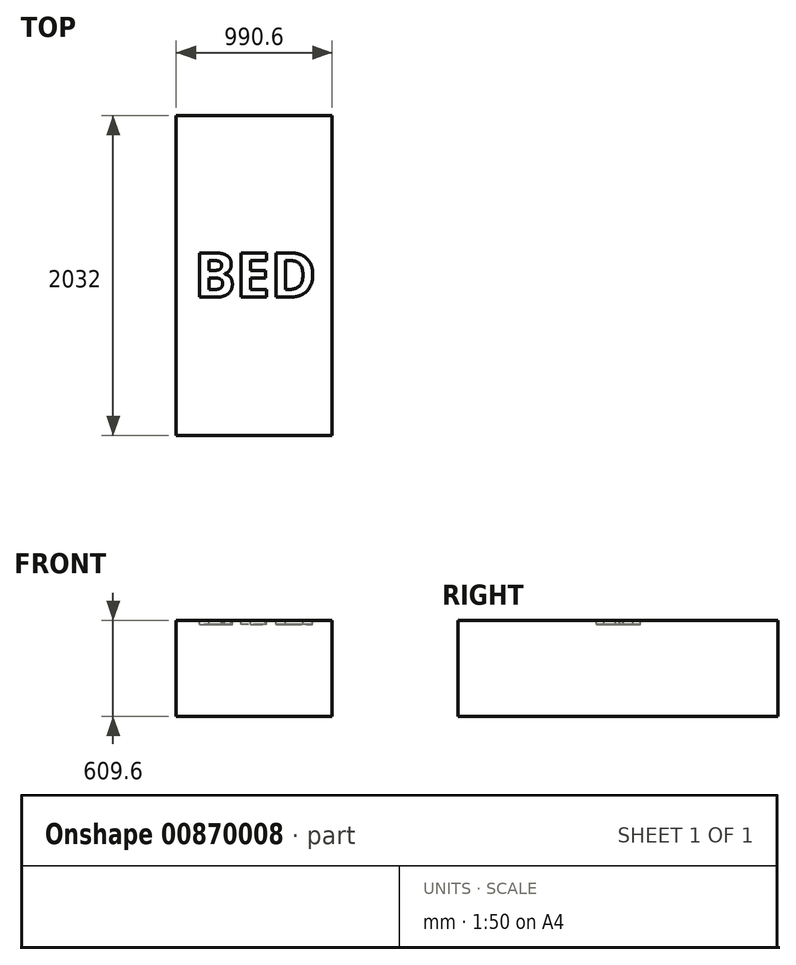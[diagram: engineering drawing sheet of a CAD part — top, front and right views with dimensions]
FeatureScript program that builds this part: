
annotation { "Feature Type Name" : "Feature", "Feature Type Description" : "" }
export const myFeature = defineFeature(function(context is Context, id is Id, definition is map)
    precondition{}
    {
        {
            var Q0;
            Q0=qCreatedBy(makeId("Top.planeOp"),FACE);
            var sketch = newSketch(context, id + "F0", { "sketchPlane" : qUnion([Q0])});
            skLineSegment(sketch, "E0.bottom", {"start": v(0, 0) * mm, "end": v(990.6, 0) * mm});
            skLineSegment(sketch, "E0.top", {"start": v(0, 2032) * mm, "end": v(990.6, 2032) * mm});
            skLineSegment(sketch, "E0.left", {"start": v(0, 0) * mm, "end": v(0, 2032) * mm});
            skLineSegment(sketch, "E0.right", {"start": v(990.6, 0) * mm, "end": v(990.6, 2032) * mm});
            skSolve(sketch);
        }
        {
            var Q0;
            Q0 = qSketchRegion(id + "F0", true);
            extrude(context, id + "F1", {"entities" : qUnion([Q0]), "depth" : 609.6 * mm, "offsetDistance" : 25.4 * mm});
        }
        {
            var Q0;
            Q0=makeQuery(id+"F1.opExtrude","CAP_FACE",FACE,{"disambiguationData":[OSD([sQuery(id+"F0.wireOp",EDGE,"E0.bottom"),sQuery(id+"F0.wireOp",EDGE,"E0.top"),sQuery(id+"F0.wireOp",EDGE,"E0.left"),sQuery(id+"F0.wireOp",EDGE,"E0.right")])],"isStart":false});
            var sketch = newSketch(context, id + "F2", { "sketchPlane" : qUnion([Q0])});
            skText(sketch, "E1", { "text": "BED", "fontName": "OpenSans-Bold.ttf"});
            const initialGuessF2  = {"E1": [0.1126, 0.87804, 1, 0, 0.28392]};
            skSetInitialGuess(sketch, initialGuessF2);
            skSolve(sketch);
        }
        {
            var Q0;
            Q0 = qSketchRegion(id + "F2", true);
            extrude(context, id + "F3", {"entities" : qUnion([Q0]), "operationType" : NewBodyOperationType.REMOVE, "oppositeDirection" : true, "depth" : 25.4 * mm, "offsetDistance" : 25.4 * mm});
        }
    });
